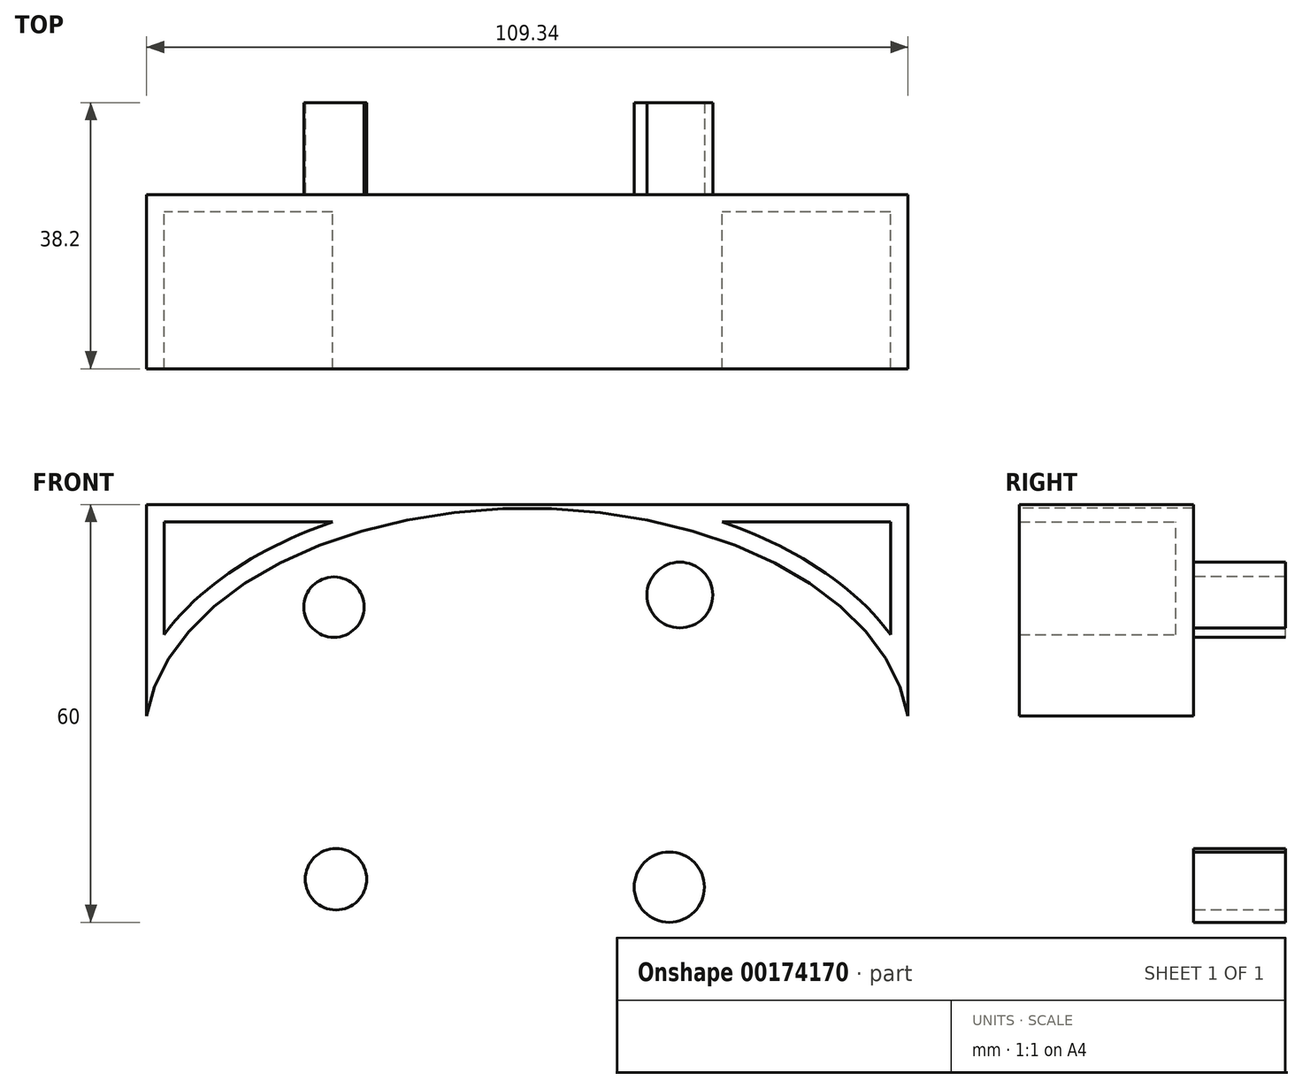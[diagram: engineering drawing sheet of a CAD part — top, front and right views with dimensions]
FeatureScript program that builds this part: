
annotation { "Feature Type Name" : "Feature", "Feature Type Description" : "" }
export const myFeature = defineFeature(function(context is Context, id is Id, definition is map)
    precondition{}
    {
        {
            var Q0;
            Q0=qCreatedBy(makeId("Front.planeOp"),FACE);
            var sketch = newSketch(context, id + "F0", { "sketchPlane" : qUnion([Q0])});
            skLineSegment(sketch, "E0.bottom", {"start": v(54.67, -33.7) * mm, "end": v(-54.67, -33.7) * mm});
            skLineSegment(sketch, "E0.top", {"start": v(54.67, 33.7) * mm, "end": v(-54.67, 33.7) * mm});
            skLineSegment(sketch, "E0.left", {"start": v(54.67, -33.7) * mm, "end": v(54.67, 33.7) * mm});
            skLineSegment(sketch, "E0.right", {"start": v(-54.67, -33.7) * mm, "end": v(-54.67, 33.7) * mm});
            skPoint(sketch, "E0.middle", {"position": v(0, 0) * mm});
            skEllipse(sketch, "E1", {"center": v(0, 0) * mm, "majorRadius": 54.96 * mm, "minorRadius": 33.18 * mm, "majorAxis": v(1, 0)});
            skSolve(sketch);
        }
        {
            var Q0;
            {var subQ0=sQuery(id+"F0.wireOp",EDGE,"E1");var subQ1=sQuery(id+"F0.wireOp",EDGE,"E0.left");var subQ2=makeQuery(id+"F0.imprint","INTERSECT",VERTEX,{"disambiguationData":[OD(0.0)],"derivedFrom":[subQ1,subQ0]});Q0=makeQuery(id+"F0.imprint","IMPRINT",FACE,{"disambiguationData":[TD([[makeQuery(id+"F0.imprint","IMPRINT",EDGE,{"disambiguationData":[TD([[subQ2,-1.0]])],"derivedFrom":subQ1}),1.0]])]});}
            extrude(context, id + "F1", {"entities" : qUnion([Q0]), "depth" : 25 * mm});
        }
        {
            var Q0;
            Q0=makeQuery(id+"F1.opExtrude","CAP_FACE",FACE,{"disambiguationData":[OSD([sQuery(id+"F0.wireOp",EDGE,"E0.left"),sQuery(id+"F0.wireOp",EDGE,"E0.right"),sQuery(id+"F0.wireOp",EDGE,"E1")])],"isStart":false});
            shell(context, id + "F2", {"entities" : qUnion([Q0]), "thickness" : 2.5 * mm});
        }
        {
            var Q0;
            Q0=qCreatedBy(makeId("Front.planeOp"),FACE);
            var sketch = newSketch(context, id + "F3", { "sketchPlane" : qUnion([Q0])});
            skCircle(sketch, "E2", {"center": v(-27.48, 18.7) * mm, "radius": 4.48 * mm});
            skCircle(sketch, "E3", {"center": v(21.53, 20.4) * mm, "radius": 4.82 * mm});
            skCircle(sketch, "E4", {"center": v(-27.76, -20.4) * mm, "radius": 4.57 * mm});
            skPoint(sketch, "E5.center.orphan", {"position": v(31.73, 0) * mm});
            skLineSegment(sketch, "E6.bottom", {"start": v(23.51, -9.35) * mm, "end": v(26.91, -9.35) * mm});
            skLineSegment(sketch, "E6.top", {"start": v(23.51, 9.35) * mm, "end": v(26.91, 9.35) * mm});
            skLineSegment(sketch, "E6.left", {"start": v(23.51, -9.35) * mm, "end": v(23.51, 9.35) * mm});
            skLineSegment(sketch, "E6.right", {"start": v(26.91, -9.35) * mm, "end": v(26.91, 9.35) * mm});
            skPoint(sketch, "E6.middle", {"position": v(25.21, 0) * mm});
            skLineSegment(sketch, "E7.bottom", {"start": v(13.31, 0) * mm, "end": v(33.7, 0) * mm});
            skPoint(sketch, "E7.middle", {"position": v(23.51, -9.35) * mm});
            skLineSegment(sketch, "E8.bottom", {"start": v(11.33, -9.35) * mm, "end": v(15.3, -9.35) * mm});
            skLineSegment(sketch, "E8.top", {"start": v(11.33, 9.35) * mm, "end": v(15.3, 9.35) * mm});
            skLineSegment(sketch, "E8.left", {"start": v(11.33, -9.35) * mm, "end": v(11.33, 9.35) * mm});
            skLineSegment(sketch, "E8.right", {"start": v(15.3, -9.35) * mm, "end": v(15.3, 9.35) * mm});
            skPoint(sketch, "E8.middle", {"position": v(13.31, 0) * mm});
            skPoint(sketch, "E8.cornerSnap0", {"position": v(13.31, -9.35) * mm});
            skLineSegment(sketch, "E9.bottom", {"start": v(-13.88, -9.35) * mm, "end": v(-17.28, -9.35) * mm});
            skLineSegment(sketch, "E9.top", {"start": v(-13.88, 9.35) * mm, "end": v(-17.28, 9.35) * mm});
            skLineSegment(sketch, "E9.left", {"start": v(-13.88, -9.35) * mm, "end": v(-13.88, 9.35) * mm});
            skLineSegment(sketch, "E9.right", {"start": v(-17.28, -9.35) * mm, "end": v(-17.28, 9.35) * mm});
            skPoint(sketch, "E9.middle", {"position": v(-15.58, 0) * mm});
            skLineSegment(sketch, "E10.left", {"start": v(-5.67, -9.35) * mm, "end": v(-5.67, -8.5) * mm});
            skPoint(sketch, "E10.middle", {"position": v(-13.88, -8.5) * mm});
            skLineSegment(sketch, "E11.bottom", {"start": v(-5.67, -9.35) * mm, "end": v(-5.67, -9.35) * mm});
            skLineSegment(sketch, "E11.top", {"start": v(-5.67, -21.25) * mm, "end": v(-5.67, -21.25) * mm});
            skPoint(sketch, "E11.middle", {"position": v(-5.67, -15.3) * mm});
            skPoint(sketch, "E11.cornerSnap0", {"position": v(-5.67, -8.5) * mm});
            skLineSegment(sketch, "E12.bottom", {"start": v(-3.12, -9.35) * mm, "end": v(3.12, -9.35) * mm});
            skLineSegment(sketch, "E12.top", {"start": v(-3.12, 9.35) * mm, "end": v(3.12, 9.35) * mm});
            skLineSegment(sketch, "E12.left", {"start": v(-3.12, -9.35) * mm, "end": v(-3.12, 9.35) * mm});
            skLineSegment(sketch, "E12.right", {"start": v(3.12, -9.35) * mm, "end": v(3.12, 9.35) * mm});
            skPoint(sketch, "E12.middle", {"position": v(0, 0) * mm});
            skPoint(sketch, "E13.middle", {"position": v(-30.31, -1.7) * mm});
            skPoint(sketch, "E13.left.end.orphan", {"position": v(-33.43, 1.13) * mm});
            skPoint(sketch, "E13.left.start.orphan", {"position": v(-33.43, -4.53) * mm});
            skPoint(sketch, "E13.right.end.orphan", {"position": v(-27.2, 1.13) * mm});
            skPoint(sketch, "E13.right.start.orphan", {"position": v(-27.2, -4.53) * mm});
            skPoint(sketch, "E10.bottom.end.orphan", {"position": v(-22.1, -15.3) * mm});
            skPoint(sketch, "E10.top.end.orphan", {"position": v(-22.1, -1.7) * mm});
            skPoint(sketch, "E14.orphan", {"position": v(-5.67, -1.7) * mm});
            skPoint(sketch, "E15.orphan", {"position": v(13.31, -18.7) * mm});
            skPoint(sketch, "E7.top.end.orphan", {"position": v(33.7, -18.7) * mm});
            skLineSegment(sketch, "E16.bottom", {"start": v(-33.43, -11.33) * mm, "end": v(-27.2, -11.33) * mm});
            skLineSegment(sketch, "E16.top", {"start": v(-33.43, 7.93) * mm, "end": v(-27.2, 7.93) * mm});
            skLineSegment(sketch, "E16.left", {"start": v(-33.43, -11.33) * mm, "end": v(-33.43, 7.93) * mm});
            skLineSegment(sketch, "E16.right", {"start": v(-27.2, -11.33) * mm, "end": v(-27.2, 7.93) * mm});
            skCircle(sketch, "E17", {"center": v(20.4, -21.25) * mm, "radius": 5.04 * mm});
            skSolve(sketch);
        }
        {
            var Q0;
            Q0 = qSketchRegion(id + "F3", true);
            extrude(context, id + "F4", {"entities" : qUnion([Q0]), "operationType" : NewBodyOperationType.ADD, "depth" : 6.2 * mm});
        }
        {
            var Q0;
            Q0 = qSketchRegion(id + "F3", true);
            extrude(context, id + "F5", {"entities" : qUnion([Q0]), "operationType" : NewBodyOperationType.REMOVE, "oppositeDirection" : true, "depth" : 71.9 * mm, "hasSecondDirection" : true, "secondDirectionBound" : SecondDirectionBoundingType.THROUGH_ALL, "secondDirectionOppositeDirection" : false, "secondDirectionDepth" : 25 * mm});
        }
        {
            var Q0;
            Q0=qCreatedBy(makeId("Front.planeOp"),FACE);
            var sketch = newSketch(context, id + "F6", { "sketchPlane" : qUnion([Q0])});
            skCircle(sketch, "E18", {"center": v(21.91, 20.7) * mm, "radius": 4.72 * mm});
            skCircle(sketch, "E19", {"center": v(-27.76, 18.98) * mm, "radius": 4.33 * mm});
            skArc(sketch, "E20", {"start": v(-31.88, -19.98) * mm, "mid": v(-27.48, -20.11) * mm, "end": v(-23.1, -19.7) * mm});
            skCircle(sketch, "E21", {"center": v(-27.48, -20.11) * mm, "radius": 4.4 * mm});
            skCircle(sketch, "E22", {"center": v(20.4, -21.25) * mm, "radius": 5.04 * mm});
            skSolve(sketch);
        }
        {
            var Q0;
            Q0 = qSketchRegion(id + "F6", true);
            extrude(context, id + "F7", {"entities" : qUnion([Q0]), "operationType" : NewBodyOperationType.ADD, "oppositeDirection" : true, "depth" : 13.2 * mm});
        }
    });
